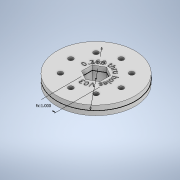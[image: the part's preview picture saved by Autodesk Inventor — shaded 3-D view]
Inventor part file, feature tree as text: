
AUTODESK INVENTOR PART (.ipt)
format: ipt  version: 2022.2 (Build 262287010, 287A)  size: 839,680 bytes
history: native  units: in
note: dims shown in document units (in); Inventor stores cm internally (conversion verified against a paired STEP export)
features: sketch x6, extrude x4, emboss x2, hole x1, pattern_circular x1
ambient origin geometry x8: Origin, YZ Plane, XZ Plane, XY Plane, X Axis, Y Axis, Z Axis, Center Point
bodies: Solid1 (feature_tree)
feature tree (14):
  sketch  "Sketch1"  dims[d0=4.25in d1=1.0in]
  extrude  "Extrusion1"  Depth=1.0in
  extrude  "Extrusion2"  Depth=0.25in
  emboss  "Emboss1"
  extrude  "Extrusion3"  Depth=2.0in
  hole  "Hole2"  [1 undecoded]
  pattern_circular  "Circular Pattern1"  Count=8 Angle=360.0deg
  emboss  "Emboss4"
  extrude  "Extrusion4"  Depth=0.05in
  sketch  "Sketch3"  dims[d2=0.25in d3=0.0in d16=1.24in]
  sketch  "Sketch4"  dims[d17=0.75in d18=0.0in d19=2.0in]
  sketch  "Sketch8"  dims[d20=0.05in d21=0.0in d28=0.25in]
  sketch  "Sketch9"  dims[d29=0.0in]
  sketch  "Sketch10"  dims[d30=2.75in d31=0.266in d32=0.75in d33=0.65in d34=0.25in d35=0.5635in d36=1.0in d37=0.8108in d38=3.1496in d39=360.0deg d41=1.5in d42=0.05in d43=0.0in d44=0.0in d45=0.0in d46=0.5in d47=0.0344in]
note: 1 required parameter value undecoded (feature->parameter linkage not recoverable at this tier; creation-order binding heuristic only, values carry confidence <= 0.55)
